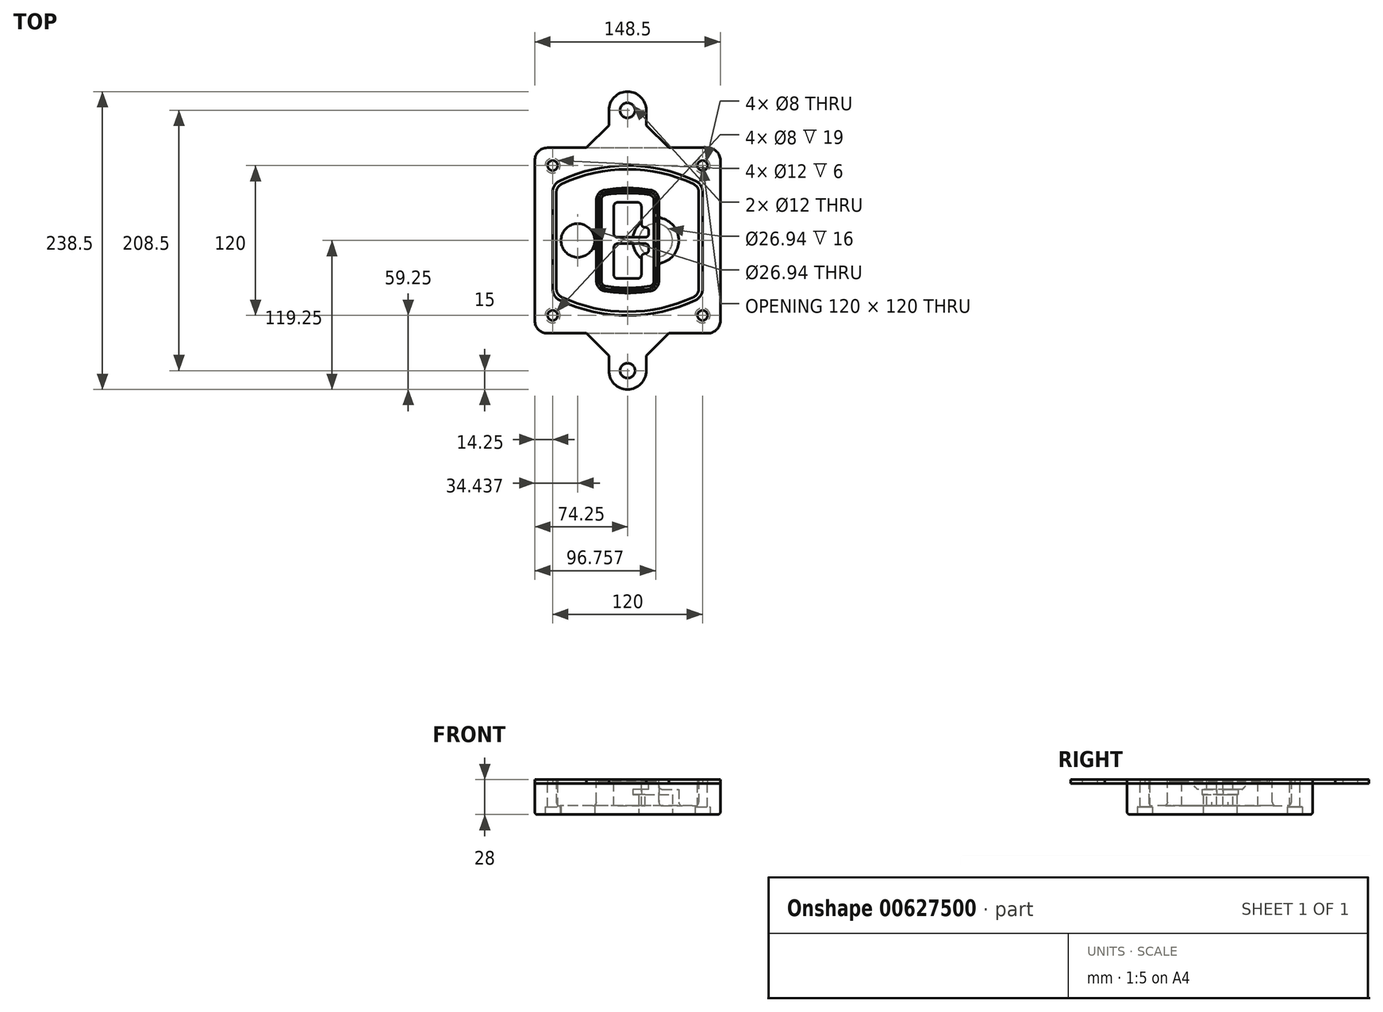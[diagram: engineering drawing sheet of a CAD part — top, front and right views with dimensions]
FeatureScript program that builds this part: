
annotation { "Feature Type Name" : "Feature", "Feature Type Description" : "" }
export const myFeature = defineFeature(function(context is Context, id is Id, definition is map)
    precondition{}
    {
        {
            var Q0;
            Q0=qCreatedBy(makeId("Top.planeOp"),FACE);
            var sketch = newSketch(context, id + "F0", { "sketchPlane" : qUnion([Q0])});
            skPoint(sketch, "E0.rect.middle", {"position": v(0, 0) * mm});
            skLineSegment(sketch, "E1.bottom", {"start": v(-64.25, -74.25) * mm, "end": v(64.25, -74.25) * mm});
            skLineSegment(sketch, "E1.top", {"start": v(-64.25, 74.25) * mm, "end": v(64.25, 74.25) * mm});
            skLineSegment(sketch, "E1.left", {"start": v(-74.25, -64.25) * mm, "end": v(-74.25, 64.25) * mm});
            skLineSegment(sketch, "E1.right", {"start": v(74.25, -64.25) * mm, "end": v(74.25, 64.25) * mm});
            skLineSegment(sketch, "E2", {"start": v(-74.25, 74.25) * mm, "end": v(74.25, -74.25) * mm, "construction": true});
            skLineSegment(sketch, "E3", {"start": v(74.25, 74.25) * mm, "end": v(-74.25, -74.25) * mm, "construction": true});
            skCircle(sketch, "E4", {"center": v(-60, 60) * mm, "radius": 4 * mm});
            skCircle(sketch, "E5", {"center": v(60, 60) * mm, "radius": 4 * mm});
            skCircle(sketch, "E6", {"center": v(60, -60) * mm, "radius": 4 * mm});
            skCircle(sketch, "E7", {"center": v(-60, -60) * mm, "radius": 4 * mm});
            skLineSegment(sketch, "E8", {"start": v(-60, 60) * mm, "end": v(60, 60) * mm, "construction": true});
            skLineSegment(sketch, "E9", {"start": v(60, 60) * mm, "end": v(60, -60) * mm, "construction": true});
            skLineSegment(sketch, "E10", {"start": v(60, -60) * mm, "end": v(-60, -60) * mm, "construction": true});
            skLineSegment(sketch, "E11", {"start": v(-60, -60) * mm, "end": v(-60, 60) * mm, "construction": true});
            skLineSegment(sketch, "E12", {"start": v(-60, 38.83) * mm, "end": v(-60, -38.83) * mm});
            skLineSegment(sketch, "E13", {"start": v(60, 38.83) * mm, "end": v(60, -38.83) * mm});
            skArc(sketch, "E14", {"start": v(54.26, 47.88) * mm, "mid": v(0, 60) * mm, "end": v(-54.26, 47.88) * mm});
            skArc(sketch, "E15", {"start": v(-54.26, -47.88) * mm, "mid": v(0, -60) * mm, "end": v(54.26, -47.88) * mm});
            skLineSegment(sketch, "E16", {"start": v(-60, 0) * mm, "end": v(60, 0) * mm, "construction": true});
            skPoint(sketch, "E17.visualSharp", {"position": v(-60, -45) * mm});
            skArc(sketch, "E17.filletArc", {"start": v(-60, -38.83) * mm, "mid": v(-58.44, -44.2) * mm, "end": v(-54.26, -47.88) * mm});
            skPoint(sketch, "E18.visualSharp", {"position": v(-60, 45) * mm});
            skArc(sketch, "E18.filletArc", {"start": v(-54.26, 47.88) * mm, "mid": v(-58.44, 44.2) * mm, "end": v(-60, 38.83) * mm});
            skPoint(sketch, "E19.visualSharp", {"position": v(60, 45) * mm});
            skArc(sketch, "E19.filletArc", {"start": v(60, 38.83) * mm, "mid": v(58.44, 44.2) * mm, "end": v(54.26, 47.88) * mm});
            skPoint(sketch, "E20.visualSharp", {"position": v(60, -45) * mm});
            skArc(sketch, "E20.filletArc", {"start": v(54.26, -47.88) * mm, "mid": v(58.44, -44.2) * mm, "end": v(60, -38.83) * mm});
            skPoint(sketch, "E21.visualSharp", {"position": v(-74.25, 74.25) * mm});
            skArc(sketch, "E21.filletArc", {"start": v(-64.25, 74.25) * mm, "mid": v(-71.32, 71.32) * mm, "end": v(-74.25, 64.25) * mm});
            skPoint(sketch, "E22.visualSharp", {"position": v(74.25, 74.25) * mm});
            skArc(sketch, "E22.filletArc", {"start": v(74.25, 64.25) * mm, "mid": v(71.32, 71.32) * mm, "end": v(64.25, 74.25) * mm});
            skPoint(sketch, "E23.visualSharp", {"position": v(74.25, -74.25) * mm});
            skArc(sketch, "E23.filletArc", {"start": v(64.25, -74.25) * mm, "mid": v(71.32, -71.32) * mm, "end": v(74.25, -64.25) * mm});
            skPoint(sketch, "E24.visualSharp", {"position": v(-74.25, -74.25) * mm});
            skArc(sketch, "E24.filletArc", {"start": v(-74.25, -64.25) * mm, "mid": v(-71.32, -71.32) * mm, "end": v(-64.25, -74.25) * mm});
            skArc(sketch, "E25.0", {"start": v(57, 38.83) * mm, "mid": v(55.9, 42.58) * mm, "end": v(52.98, 45.17) * mm});
            skLineSegment(sketch, "E25.1", {"start": v(57, 38.83) * mm, "end": v(57, -38.83) * mm});
            skArc(sketch, "E25.2", {"start": v(52.98, -45.17) * mm, "mid": v(55.9, -42.58) * mm, "end": v(57, -38.83) * mm});
            skArc(sketch, "E25.3", {"start": v(-52.98, -45.17) * mm, "mid": v(0, -57) * mm, "end": v(52.98, -45.17) * mm});
            skArc(sketch, "E25.4", {"start": v(-57, -38.83) * mm, "mid": v(-55.9, -42.58) * mm, "end": v(-52.98, -45.17) * mm});
            skArc(sketch, "E25.5", {"start": v(52.98, 45.17) * mm, "mid": v(0, 57) * mm, "end": v(-52.98, 45.17) * mm});
            skLineSegment(sketch, "E25.6", {"start": v(-57, 38.83) * mm, "end": v(-57, -38.83) * mm});
            skArc(sketch, "E25.7", {"start": v(-52.98, 45.17) * mm, "mid": v(-55.9, 42.58) * mm, "end": v(-57, 38.83) * mm});
            skArc(sketch, "E26.0", {"start": v(-55.96, 51.5) * mm, "mid": v(-61.82, 46.33) * mm, "end": v(-64, 38.83) * mm});
            skArc(sketch, "E26.1", {"start": v(55.96, 51.5) * mm, "mid": v(0, 64) * mm, "end": v(-55.96, 51.5) * mm});
            skArc(sketch, "E26.2", {"start": v(64, 38.83) * mm, "mid": v(61.82, 46.33) * mm, "end": v(55.96, 51.5) * mm});
            skLineSegment(sketch, "E26.3", {"start": v(64, 38.83) * mm, "end": v(64, -38.83) * mm});
            skArc(sketch, "E26.4", {"start": v(55.96, -51.5) * mm, "mid": v(61.82, -46.33) * mm, "end": v(64, -38.83) * mm});
            skLineSegment(sketch, "E26.5", {"start": v(-64, 38.83) * mm, "end": v(-64, -38.83) * mm});
            skArc(sketch, "E26.6", {"start": v(-55.96, -51.5) * mm, "mid": v(0, -64) * mm, "end": v(55.96, -51.5) * mm});
            skArc(sketch, "E26.7", {"start": v(-64, -38.83) * mm, "mid": v(-61.82, -46.33) * mm, "end": v(-55.96, -51.5) * mm});
            skSolve(sketch);
        }
        {
            var Q0;
            Q0=makeQuery(id+"F0.imprint","IMPRINT",FACE,{"disambiguationData":[TD([[makeQuery(id+"F0.imprint","IMPRINT",EDGE,{"derivedFrom":sQuery(id+"F0.wireOp",EDGE,"E1.bottom")}),1.0]])]});
            var Q1;
            Q1=makeQuery(id+"F0.imprint","IMPRINT",FACE,{"disambiguationData":[TD([[makeQuery(id+"F0.imprint","IMPRINT",EDGE,{"derivedFrom":sQuery(id+"F0.wireOp",EDGE,"E12")}),1.0]])]});
            var Q2;
            Q2=makeQuery(id+"F0.imprint","IMPRINT",FACE,{"disambiguationData":[TD([[makeQuery(id+"F0.imprint","IMPRINT",EDGE,{"derivedFrom":sQuery(id+"F0.wireOp",EDGE,"E25.0")}),1.0]])]});
            var Q3;
            Q3=makeQuery(id+"F0.imprint","IMPRINT",FACE,{"disambiguationData":[TD([[makeQuery(id+"F0.imprint","IMPRINT",EDGE,{"derivedFrom":sQuery(id+"F0.wireOp",EDGE,"E12")}),-1.0]])]});
            extrude(context, id + "F1", {"entities" : qUnion([Q0, Q1, Q2, Q3]), "oppositeDirection" : true, "depth" : 25 * mm});
        }
        {
            var Q0;
            Q0=makeQuery(id+"F0.imprint","IMPRINT",FACE,{"disambiguationData":[TD([[makeQuery(id+"F0.imprint","IMPRINT",EDGE,{"derivedFrom":sQuery(id+"F0.wireOp",EDGE,"E12")}),1.0]])]});
            extrude(context, id + "F2", {"entities" : qUnion([Q0]), "operationType" : NewBodyOperationType.ADD, "depth" : 3 * mm});
        }
        {
            var Q0;
            Q0=makeQuery(id+"F0.imprint","IMPRINT",FACE,{"disambiguationData":[TD([[makeQuery(id+"F0.imprint","IMPRINT",EDGE,{"derivedFrom":sQuery(id+"F0.wireOp",EDGE,"E25.0")}),1.0]])]});
            extrude(context, id + "F3", {"entities" : qUnion([Q0]), "operationType" : NewBodyOperationType.REMOVE, "oppositeDirection" : true, "depth" : 18 * mm});
        }
        {
            var Q0;
            Q0=makeQuery(id+"F2.opExtrude","CAP_FACE",FACE,{"disambiguationData":[OSD([sQuery(id+"F0.wireOp",EDGE,"E12"),sQuery(id+"F0.wireOp",EDGE,"E13"),sQuery(id+"F0.wireOp",EDGE,"E14"),sQuery(id+"F0.wireOp",EDGE,"E15"),sQuery(id+"F0.wireOp",EDGE,"E17.filletArc"),sQuery(id+"F0.wireOp",EDGE,"E18.filletArc"),sQuery(id+"F0.wireOp",EDGE,"E19.filletArc"),sQuery(id+"F0.wireOp",EDGE,"E20.filletArc"),sQuery(id+"F0.wireOp",EDGE,"E25.0"),sQuery(id+"F0.wireOp",EDGE,"E25.1"),sQuery(id+"F0.wireOp",EDGE,"E25.2"),sQuery(id+"F0.wireOp",EDGE,"E25.3"),sQuery(id+"F0.wireOp",EDGE,"E25.4"),sQuery(id+"F0.wireOp",EDGE,"E25.5"),sQuery(id+"F0.wireOp",EDGE,"E25.6"),sQuery(id+"F0.wireOp",EDGE,"E25.7")])],"isStart":false});
            var sketch = newSketch(context, id + "F4", { "sketchPlane" : qUnion([Q0])});
            skArc(sketch, "E27.0", {"start": v(-18.34, -40.45) * mm, "mid": v(0, -42) * mm, "end": v(18.34, -40.45) * mm});
            skArc(sketch, "E28.0", {"start": v(18.34, 40.45) * mm, "mid": v(0, 42) * mm, "end": v(-18.34, 40.45) * mm});
            skLineSegment(sketch, "E29", {"start": v(-25, 32.57) * mm, "end": v(-25, -32.57) * mm});
            skLineSegment(sketch, "E30", {"start": v(25, 32.57) * mm, "end": v(25, -32.57) * mm});
            skLineSegment(sketch, "E31", {"start": v(-25, 39.1) * mm, "end": v(25, 39.1) * mm, "construction": true});
            skLineSegment(sketch, "E32", {"start": v(-25, -39.1) * mm, "end": v(25, -39.1) * mm, "construction": true});
            skPoint(sketch, "E33.visualSharp", {"position": v(-25, 39.1) * mm});
            skArc(sketch, "E33.filletArc", {"start": v(-18.34, 40.45) * mm, "mid": v(-23.11, 37.73) * mm, "end": v(-25, 32.57) * mm});
            skPoint(sketch, "E34.visualSharp", {"position": v(25, 39.1) * mm});
            skArc(sketch, "E34.filletArc", {"start": v(25, 32.57) * mm, "mid": v(23.11, 37.73) * mm, "end": v(18.34, 40.45) * mm});
            skPoint(sketch, "E35.visualSharp", {"position": v(25, -39.1) * mm});
            skArc(sketch, "E35.filletArc", {"start": v(18.34, -40.45) * mm, "mid": v(23.11, -37.73) * mm, "end": v(25, -32.57) * mm});
            skPoint(sketch, "E36.visualSharp", {"position": v(-25, -39.1) * mm});
            skArc(sketch, "E36.filletArc", {"start": v(-25, -32.57) * mm, "mid": v(-23.11, -37.73) * mm, "end": v(-18.34, -40.45) * mm});
            skArc(sketch, "E37.0", {"start": v(52.98, 45.17) * mm, "mid": v(0, 57) * mm, "end": v(-52.98, 45.17) * mm});
            skArc(sketch, "E37.1", {"start": v(-52.98, 45.17) * mm, "mid": v(-55.9, 42.58) * mm, "end": v(-57, 38.83) * mm});
            skLineSegment(sketch, "E37.2", {"start": v(-57, 38.83) * mm, "end": v(-57, -38.83) * mm});
            skArc(sketch, "E37.3", {"start": v(-57, -38.83) * mm, "mid": v(-55.9, -42.58) * mm, "end": v(-52.98, -45.17) * mm});
            skArc(sketch, "E37.4", {"start": v(-52.98, -45.17) * mm, "mid": v(0, -57) * mm, "end": v(52.98, -45.17) * mm});
            skArc(sketch, "E37.5", {"start": v(52.98, -45.17) * mm, "mid": v(55.9, -42.58) * mm, "end": v(57, -38.83) * mm});
            skLineSegment(sketch, "E37.6", {"start": v(57, 38.83) * mm, "end": v(57, -38.83) * mm});
            skArc(sketch, "E37.7", {"start": v(57, 38.83) * mm, "mid": v(55.9, 42.58) * mm, "end": v(52.98, 45.17) * mm});
            skLineSegment(sketch, "E38.0", {"start": v(23, 32.57) * mm, "end": v(23, -32.57) * mm});
            skArc(sketch, "E38.1", {"start": v(18, -38.48) * mm, "mid": v(21.58, -36.44) * mm, "end": v(23, -32.57) * mm});
            skArc(sketch, "E38.2", {"start": v(-18, -38.48) * mm, "mid": v(0, -40) * mm, "end": v(18, -38.48) * mm});
            skArc(sketch, "E38.3", {"start": v(-23, -32.57) * mm, "mid": v(-21.58, -36.44) * mm, "end": v(-18, -38.48) * mm});
            skLineSegment(sketch, "E38.4", {"start": v(-23, 32.57) * mm, "end": v(-23, -32.57) * mm});
            skArc(sketch, "E38.5", {"start": v(23, 32.57) * mm, "mid": v(21.58, 36.44) * mm, "end": v(18, 38.48) * mm});
            skArc(sketch, "E38.6", {"start": v(-18, 38.48) * mm, "mid": v(-21.58, 36.44) * mm, "end": v(-23, 32.57) * mm});
            skArc(sketch, "E38.7", {"start": v(18, 38.48) * mm, "mid": v(0, 40) * mm, "end": v(-18, 38.48) * mm});
            skArc(sketch, "E39.0", {"start": v(21, 32.57) * mm, "mid": v(20.06, 35.15) * mm, "end": v(17.67, 36.5) * mm});
            skLineSegment(sketch, "E39.1", {"start": v(21, 32.57) * mm, "end": v(21, -32.57) * mm});
            skArc(sketch, "E39.2", {"start": v(17.67, -36.5) * mm, "mid": v(20.06, -35.15) * mm, "end": v(21, -32.57) * mm});
            skArc(sketch, "E39.3", {"start": v(-17.67, -36.5) * mm, "mid": v(0, -38) * mm, "end": v(17.67, -36.5) * mm});
            skArc(sketch, "E39.4", {"start": v(-21, -32.57) * mm, "mid": v(-20.06, -35.15) * mm, "end": v(-17.67, -36.5) * mm});
            skArc(sketch, "E39.5", {"start": v(17.67, 36.5) * mm, "mid": v(0, 38) * mm, "end": v(-17.67, 36.5) * mm});
            skLineSegment(sketch, "E39.6", {"start": v(-21, 32.57) * mm, "end": v(-21, -32.57) * mm});
            skArc(sketch, "E39.7", {"start": v(-17.67, 36.5) * mm, "mid": v(-20.06, 35.15) * mm, "end": v(-21, 32.57) * mm});
            skLineSegment(sketch, "E40", {"start": v(-25, 0) * mm, "end": v(25, 0) * mm, "construction": true});
            skLineSegment(sketch, "E41", {"start": v(-11, 5.5) * mm, "end": v(-11, 27.5) * mm});
            skLineSegment(sketch, "E42", {"start": v(-8, 30.5) * mm, "end": v(8, 30.5) * mm});
            skLineSegment(sketch, "E43", {"start": v(11, 27.5) * mm, "end": v(11, 13.5) * mm});
            skLineSegment(sketch, "E44", {"start": v(14, 10.5) * mm, "end": v(14, 10.5) * mm});
            skLineSegment(sketch, "E45", {"start": v(17, 7.5) * mm, "end": v(17, 5.5) * mm});
            skLineSegment(sketch, "E46", {"start": v(14, 2.5) * mm, "end": v(-8, 2.5) * mm});
            skPoint(sketch, "E47.visualSharp", {"position": v(-11, 30.5) * mm});
            skArc(sketch, "E47.filletArc", {"start": v(-8, 30.5) * mm, "mid": v(-10.12, 29.62) * mm, "end": v(-11, 27.5) * mm});
            skPoint(sketch, "E48.visualSharp", {"position": v(11, 30.5) * mm});
            skArc(sketch, "E48.filletArc", {"start": v(11, 27.5) * mm, "mid": v(10.12, 29.62) * mm, "end": v(8, 30.5) * mm});
            skPoint(sketch, "E49.visualSharp", {"position": v(11, 10.5) * mm});
            skArc(sketch, "E49.filletArc", {"start": v(11, 13.5) * mm, "mid": v(11.88, 11.38) * mm, "end": v(14, 10.5) * mm});
            skPoint(sketch, "E50.visualSharp", {"position": v(17, 10.5) * mm});
            skArc(sketch, "E50.filletArc", {"start": v(17, 7.5) * mm, "mid": v(16.12, 9.62) * mm, "end": v(14, 10.5) * mm});
            skPoint(sketch, "E51.visualSharp", {"position": v(17, 2.5) * mm});
            skArc(sketch, "E51.filletArc", {"start": v(14, 2.5) * mm, "mid": v(16.12, 3.38) * mm, "end": v(17, 5.5) * mm});
            skPoint(sketch, "E52.visualSharp", {"position": v(-11, 2.5) * mm});
            skArc(sketch, "E52.filletArc", {"start": v(-11, 5.5) * mm, "mid": v(-10.12, 3.38) * mm, "end": v(-8, 2.5) * mm});
            skLineSegment(sketch, "E53.0.MirrorCS", {"start": v(14, -2.5) * mm, "end": v(-8, -2.5) * mm});
            skArc(sketch, "E54.0.MirrorCS", {"start": v(-11, -5.5) * mm, "mid": v(-10.12, -3.38) * mm, "end": v(-8, -2.5) * mm});
            skLineSegment(sketch, "E55.0.MirrorCS", {"start": v(-11, -5.5) * mm, "end": v(-11, -27.5) * mm});
            skArc(sketch, "E56.0.MirrorCS", {"start": v(-8, -30.5) * mm, "mid": v(-10.12, -29.62) * mm, "end": v(-11, -27.5) * mm});
            skLineSegment(sketch, "E57.0.MirrorCS", {"start": v(-8, -30.5) * mm, "end": v(8, -30.5) * mm});
            skArc(sketch, "E58.0.MirrorCS", {"start": v(11, -27.5) * mm, "mid": v(10.12, -29.62) * mm, "end": v(8, -30.5) * mm});
            skLineSegment(sketch, "E59.0.MirrorCS", {"start": v(11, -27.5) * mm, "end": v(11, -13.5) * mm});
            skArc(sketch, "E60.0.MirrorCS", {"start": v(11, -13.5) * mm, "mid": v(11.88, -11.38) * mm, "end": v(14, -10.5) * mm});
            skArc(sketch, "E61.0.MirrorCS", {"start": v(17, -7.5) * mm, "mid": v(16.12, -9.62) * mm, "end": v(14, -10.5) * mm});
            skLineSegment(sketch, "E62.0.MirrorCS", {"start": v(17, -7.5) * mm, "end": v(17, -5.5) * mm});
            skArc(sketch, "E63.0.MirrorCS", {"start": v(14, -2.5) * mm, "mid": v(16.12, -3.38) * mm, "end": v(17, -5.5) * mm});
            skSolve(sketch);
        }
        {
            var Q0;
            Q0=makeQuery(id+"F4.imprint","IMPRINT",FACE,{"disambiguationData":[TD([[makeQuery(id+"F4.imprint","IMPRINT",EDGE,{"derivedFrom":sQuery(id+"F4.wireOp",EDGE,"E27.0")}),1.0]])]});
            var Q1;
            Q1=makeQuery(id+"F4.imprint","IMPRINT",FACE,{"disambiguationData":[TD([[makeQuery(id+"F4.imprint","IMPRINT",EDGE,{"derivedFrom":sQuery(id+"F4.wireOp",EDGE,"E38.0")}),-1.0]])]});
            var Q2;
            Q2=makeQuery(id+"F4.imprint","IMPRINT",FACE,{"disambiguationData":[TD([[makeQuery(id+"F4.imprint","IMPRINT",EDGE,{"derivedFrom":sQuery(id+"F4.wireOp",EDGE,"E39.0")}),1.0]])]});
            extrude(context, id + "F5", {"entities" : qUnion([Q0, Q1, Q2]), "operationType" : NewBodyOperationType.ADD, "endBound" : BoundingType.UP_TO_NEXT, "oppositeDirection" : true, "depth" : 25 * mm});
        }
        {
            var Q0;
            Q0=makeQuery(id+"F4.imprint","IMPRINT",FACE,{"disambiguationData":[TD([[makeQuery(id+"F4.imprint","IMPRINT",EDGE,{"derivedFrom":sQuery(id+"F4.wireOp",EDGE,"E38.0")}),-1.0]])]});
            extrude(context, id + "F6", {"entities" : qUnion([Q0]), "operationType" : NewBodyOperationType.REMOVE, "oppositeDirection" : true, "depth" : 2 * mm});
        }
        {
            var Q0;
            Q0=makeQuery(id+"F1.opExtrude","CAP_FACE",FACE,{"disambiguationData":[OSD([sQuery(id+"F0.wireOp",EDGE,"E1.bottom"),sQuery(id+"F0.wireOp",EDGE,"E1.top"),sQuery(id+"F0.wireOp",EDGE,"E1.left"),sQuery(id+"F0.wireOp",EDGE,"E1.right"),sQuery(id+"F0.wireOp",EDGE,"E4"),sQuery(id+"F0.wireOp",EDGE,"E5"),sQuery(id+"F0.wireOp",EDGE,"E6"),sQuery(id+"F0.wireOp",EDGE,"E7"),sQuery(id+"F0.wireOp",EDGE,"E21.filletArc"),sQuery(id+"F0.wireOp",EDGE,"E22.filletArc"),sQuery(id+"F0.wireOp",EDGE,"E23.filletArc"),sQuery(id+"F0.wireOp",EDGE,"E24.filletArc")])],"isStart":false});
            var sketch = newSketch(context, id + "F7", { "sketchPlane" : qUnion([Q0])});
            skCircle(sketch, "E64", {"center": v(22.5, 0) * mm, "radius": 13.47 * mm});
            skCircle(sketch, "E65", {"center": v(-39.81, 0) * mm, "radius": 13.47 * mm});
            skLineSegment(sketch, "E66", {"start": v(74.25, 0) * mm, "end": v(-74.25, 0) * mm});
            skCircle(sketch, "E67", {"center": v(22.5, 0) * mm, "radius": 18.47 * mm});
            skCircle(sketch, "E68", {"center": v(60, -60) * mm, "radius": 6 * mm});
            skCircle(sketch, "E69", {"center": v(-60, -60) * mm, "radius": 6 * mm});
            skCircle(sketch, "E70", {"center": v(-60, 60) * mm, "radius": 6 * mm});
            skCircle(sketch, "E71", {"center": v(60, 60) * mm, "radius": 6 * mm});
            skSolve(sketch);
        }
        {
            var Q0;
            {var subQ1=sQuery(id+"F7.wireOp",EDGE,"E66");var subQ4=sQuery(id+"F7.wireOp",EDGE,"E64");var subQ6=makeQuery(id+"F7.imprint","INTERSECT",VERTEX,{"disambiguationData":[OD(0.0)],"derivedFrom":[subQ4,subQ1]});Q0=makeQuery(id+"F7.imprint","IMPRINT",FACE,{"disambiguationData":[TD([[makeQuery(id+"F7.imprint","IMPRINT",EDGE,{"disambiguationData":[TD([[subQ6,-1.0]])],"derivedFrom":subQ4}),-1.0]])]});}
            var Q1;
            {var subQ0=sQuery(id+"F7.wireOp",EDGE,"E66");var subQ1=sQuery(id+"F7.wireOp",EDGE,"E64");var subQ3=makeQuery(id+"F7.imprint","INTERSECT",VERTEX,{"disambiguationData":[OD(0.0)],"derivedFrom":[subQ1,subQ0]});Q1=makeQuery(id+"F7.imprint","IMPRINT",FACE,{"disambiguationData":[TD([[makeQuery(id+"F7.imprint","IMPRINT",EDGE,{"disambiguationData":[TD([[subQ3,-1.0]])],"derivedFrom":subQ1}),1.0]])]});}
            var Q2;
            {var subQ0=sQuery(id+"F7.wireOp",EDGE,"E66");var subQ1=sQuery(id+"F7.wireOp",EDGE,"E64");var subQ3=makeQuery(id+"F7.imprint","INTERSECT",VERTEX,{"disambiguationData":[OD(0.0)],"derivedFrom":[subQ1,subQ0]});Q2=makeQuery(id+"F7.imprint","IMPRINT",FACE,{"disambiguationData":[TD([[makeQuery(id+"F7.imprint","IMPRINT",EDGE,{"disambiguationData":[TD([[subQ3,1.0]])],"derivedFrom":subQ1}),1.0]])]});}
            var Q3;
            {var subQ1=sQuery(id+"F7.wireOp",EDGE,"E66");var subQ4=sQuery(id+"F7.wireOp",EDGE,"E64");var subQ6=makeQuery(id+"F7.imprint","INTERSECT",VERTEX,{"disambiguationData":[OD(0.0)],"derivedFrom":[subQ4,subQ1]});Q3=makeQuery(id+"F7.imprint","IMPRINT",FACE,{"disambiguationData":[TD([[makeQuery(id+"F7.imprint","IMPRINT",EDGE,{"disambiguationData":[TD([[subQ6,1.0]])],"derivedFrom":subQ4}),-1.0]])]});}
            extrude(context, id + "F8", {"entities" : qUnion([Q0, Q1, Q2, Q3]), "operationType" : NewBodyOperationType.ADD, "oppositeDirection" : true, "depth" : 20 * mm});
        }
        {
            var Q0;
            {var subQ0=sQuery(id+"F7.wireOp",EDGE,"E66");var subQ1=sQuery(id+"F7.wireOp",EDGE,"E64");var subQ3=makeQuery(id+"F7.imprint","INTERSECT",VERTEX,{"disambiguationData":[OD(0.0)],"derivedFrom":[subQ1,subQ0]});Q0=makeQuery(id+"F7.imprint","IMPRINT",FACE,{"disambiguationData":[TD([[makeQuery(id+"F7.imprint","IMPRINT",EDGE,{"disambiguationData":[TD([[subQ3,-1.0]])],"derivedFrom":subQ1}),1.0]])]});}
            var Q1;
            {var subQ0=sQuery(id+"F7.wireOp",EDGE,"E66");var subQ1=sQuery(id+"F7.wireOp",EDGE,"E64");var subQ3=makeQuery(id+"F7.imprint","INTERSECT",VERTEX,{"disambiguationData":[OD(0.0)],"derivedFrom":[subQ1,subQ0]});Q1=makeQuery(id+"F7.imprint","IMPRINT",FACE,{"disambiguationData":[TD([[makeQuery(id+"F7.imprint","IMPRINT",EDGE,{"disambiguationData":[TD([[subQ3,1.0]])],"derivedFrom":subQ1}),1.0]])]});}
            extrude(context, id + "F9", {"entities" : qUnion([Q0, Q1]), "operationType" : NewBodyOperationType.REMOVE, "oppositeDirection" : true, "depth" : 16 * mm});
        }
        {
            var Q0;
            {var subQ0=sQuery(id+"F7.wireOp",EDGE,"E66");var subQ1=sQuery(id+"F7.wireOp",EDGE,"E65");var subQ3=makeQuery(id+"F7.imprint","INTERSECT",VERTEX,{"disambiguationData":[OD(0.0)],"derivedFrom":[subQ1,subQ0]});Q0=makeQuery(id+"F7.imprint","IMPRINT",FACE,{"disambiguationData":[TD([[makeQuery(id+"F7.imprint","IMPRINT",EDGE,{"disambiguationData":[TD([[subQ3,-1.0]])],"derivedFrom":subQ1}),1.0]])]});}
            var Q1;
            {var subQ0=sQuery(id+"F7.wireOp",EDGE,"E66");var subQ1=sQuery(id+"F7.wireOp",EDGE,"E65");var subQ3=makeQuery(id+"F7.imprint","INTERSECT",VERTEX,{"disambiguationData":[OD(0.0)],"derivedFrom":[subQ1,subQ0]});Q1=makeQuery(id+"F7.imprint","IMPRINT",FACE,{"disambiguationData":[TD([[makeQuery(id+"F7.imprint","IMPRINT",EDGE,{"disambiguationData":[TD([[subQ3,1.0]])],"derivedFrom":subQ1}),1.0]])]});}
            extrude(context, id + "F10", {"entities" : qUnion([Q0, Q1]), "operationType" : NewBodyOperationType.REMOVE, "oppositeDirection" : true, "depth" : 25 * mm});
        }
        {
            var Q0;
            Q0=makeQuery(id+"F7.imprint","IMPRINT",FACE,{"disambiguationData":[TD([[makeQuery(id+"F7.imprint","IMPRINT",EDGE,{"derivedFrom":sQuery(id+"F7.wireOp",EDGE,"E68")}),1.0]])]});
            var Q1;
            Q1=makeQuery(id+"F7.imprint","IMPRINT",FACE,{"disambiguationData":[TD([[makeQuery(id+"F7.imprint","IMPRINT",EDGE,{"derivedFrom":makeQuery(id+"F1.opExtrude","CAP_EDGE",EDGE,{"disambiguationData":[OSD([sQuery(id+"F0.wireOp",EDGE,"E5")])],"isStart":false})}),-1.0]])]});
            var Q2;
            Q2=makeQuery(id+"F7.imprint","IMPRINT",FACE,{"disambiguationData":[TD([[makeQuery(id+"F7.imprint","IMPRINT",EDGE,{"derivedFrom":sQuery(id+"F7.wireOp",EDGE,"E69")}),1.0]])]});
            var Q3;
            Q3=makeQuery(id+"F7.imprint","IMPRINT",FACE,{"disambiguationData":[TD([[makeQuery(id+"F7.imprint","IMPRINT",EDGE,{"derivedFrom":makeQuery(id+"F1.opExtrude","CAP_EDGE",EDGE,{"disambiguationData":[OSD([sQuery(id+"F0.wireOp",EDGE,"E4")])],"isStart":false})}),-1.0]])]});
            var Q4;
            Q4=makeQuery(id+"F7.imprint","IMPRINT",FACE,{"disambiguationData":[TD([[makeQuery(id+"F7.imprint","IMPRINT",EDGE,{"derivedFrom":sQuery(id+"F7.wireOp",EDGE,"E70")}),1.0]])]});
            var Q5;
            Q5=makeQuery(id+"F7.imprint","IMPRINT",FACE,{"disambiguationData":[TD([[makeQuery(id+"F7.imprint","IMPRINT",EDGE,{"derivedFrom":makeQuery(id+"F1.opExtrude","CAP_EDGE",EDGE,{"disambiguationData":[OSD([sQuery(id+"F0.wireOp",EDGE,"E7")])],"isStart":false})}),-1.0]])]});
            var Q6;
            Q6=makeQuery(id+"F7.imprint","IMPRINT",FACE,{"disambiguationData":[TD([[makeQuery(id+"F7.imprint","IMPRINT",EDGE,{"derivedFrom":sQuery(id+"F7.wireOp",EDGE,"E71")}),1.0]])]});
            var Q7;
            Q7=makeQuery(id+"F7.imprint","IMPRINT",FACE,{"disambiguationData":[TD([[makeQuery(id+"F7.imprint","IMPRINT",EDGE,{"derivedFrom":makeQuery(id+"F1.opExtrude","CAP_EDGE",EDGE,{"disambiguationData":[OSD([sQuery(id+"F0.wireOp",EDGE,"E6")])],"isStart":false})}),-1.0]])]});
            extrude(context, id + "F11", {"entities" : qUnion([Q0, Q1, Q2, Q3, Q4, Q5, Q6, Q7]), "operationType" : NewBodyOperationType.REMOVE, "oppositeDirection" : true, "depth" : 6 * mm});
        }
        {
            var Q0;
            Q0=makeQuery(id+"F9.boolean.opBoolean","COPY",FACE,{"derivedFrom":makeQuery(id+"F9.opExtrude","CAP_FACE",FACE,{"disambiguationData":[OSD([sQuery(id+"F7.wireOp",EDGE,"E64")])],"isStart":false})});
            var sketch = newSketch(context, id + "F12", { "sketchPlane" : qUnion([Q0])});
            skArc(sketch, "E72.0", {"start": v(11, 14.45) * mm, "mid": v(6.45, 9.13) * mm, "end": v(4.2, 2.5) * mm});
            skArc(sketch, "E72.1", {"start": v(4.2, -2.5) * mm, "mid": v(6.45, -9.13) * mm, "end": v(11, -14.45) * mm});
            skLineSegment(sketch, "E73", {"start": v(4.2, -2.5) * mm, "end": v(14, -2.5) * mm});
            skLineSegment(sketch, "E74.0", {"start": v(14, 2.5) * mm, "end": v(4.2, 2.5) * mm});
            skArc(sketch, "E74.1", {"start": v(14, 2.5) * mm, "mid": v(16.12, 3.38) * mm, "end": v(17, 5.5) * mm});
            skLineSegment(sketch, "E74.2", {"start": v(17, 7.5) * mm, "end": v(17, 5.5) * mm});
            skArc(sketch, "E74.3", {"start": v(17, 7.5) * mm, "mid": v(16.12, 9.62) * mm, "end": v(14, 10.5) * mm});
            skArc(sketch, "E74.4", {"start": v(11, 13.5) * mm, "mid": v(11.88, 11.38) * mm, "end": v(14, 10.5) * mm});
            skLineSegment(sketch, "E74.5", {"start": v(11, 14.45) * mm, "end": v(11, 13.5) * mm});
            skLineSegment(sketch, "E74.7", {"start": v(14, -2.5) * mm, "end": v(4.2, -2.5) * mm});
            skArc(sketch, "E74.8", {"start": v(14, -2.5) * mm, "mid": v(16.12, -3.38) * mm, "end": v(17, -5.5) * mm});
            skLineSegment(sketch, "E74.9", {"start": v(17, -7.5) * mm, "end": v(17, -5.5) * mm});
            skArc(sketch, "E74.10", {"start": v(17, -7.5) * mm, "mid": v(16.12, -9.62) * mm, "end": v(14, -10.5) * mm});
            skArc(sketch, "E74.11", {"start": v(11, -13.5) * mm, "mid": v(11.88, -11.38) * mm, "end": v(14, -10.5) * mm});
            skLineSegment(sketch, "E74.12", {"start": v(11, -14.45) * mm, "end": v(11, -13.5) * mm});
            skPoint(sketch, "E75.orphan", {"position": v(11, -27.5) * mm});
            skPoint(sketch, "E76.orphan", {"position": v(-8, -2.5) * mm});
            skPoint(sketch, "E77.orphan", {"position": v(-8, 2.5) * mm});
            skPoint(sketch, "E78.orphan", {"position": v(11, 27.5) * mm});
            skSolve(sketch);
        }
        {
            var Q0;
            {var subQ7=sQuery(id+"F12.wireOp",EDGE,"E72.0");var subQ14=sQuery(id+"F12.wireOp",EDGE,"E72.1");var subQ16=sQuery(id+"F12.wireOp",EDGE,"E74.1");var subQ18=sQuery(id+"F12.wireOp",EDGE,"E74.8");Q0=qUnion([makeQuery(id+"F12.imprint","IMPRINT",FACE,{"disambiguationData":[TD([[makeQuery(id+"F12.imprint","IMPRINT",EDGE,{"derivedFrom":subQ7}),1.0]])]}),makeQuery(id+"F12.imprint","IMPRINT",FACE,{"disambiguationData":[TD([[makeQuery(id+"F12.imprint","IMPRINT",EDGE,{"derivedFrom":subQ14}),1.0]])]}),makeQuery(id+"F12.imprint","IMPRINT",FACE,{"disambiguationData":[TD([[makeQuery(id+"F12.imprint","IMPRINT",EDGE,{"derivedFrom":subQ16}),1.0]])]}),makeQuery(id+"F12.imprint","IMPRINT",FACE,{"disambiguationData":[TD([[makeQuery(id+"F12.imprint","IMPRINT",EDGE,{"derivedFrom":subQ18}),-1.0]])]})]);}
            var Q1;
            Q1=makeQuery(id+"F5.boolean.opBoolean","SPLIT",FACE,{"disambiguationData":[TD([makeQuery(id+"F5.opExtrude","SWEPT_FACE",FACE,{"disambiguationData":[OSD([sQuery(id+"F4.wireOp",EDGE,"E41")])]})])],"derivedFrom":makeQuery(id+"F3.boolean.opBoolean","COPY",FACE,{"derivedFrom":makeQuery(id+"F3.opExtrude","CAP_FACE",FACE,{"disambiguationData":[OSD([sQuery(id+"F0.wireOp",EDGE,"E25.0"),sQuery(id+"F0.wireOp",EDGE,"E25.1"),sQuery(id+"F0.wireOp",EDGE,"E25.2"),sQuery(id+"F0.wireOp",EDGE,"E25.3"),sQuery(id+"F0.wireOp",EDGE,"E25.4"),sQuery(id+"F0.wireOp",EDGE,"E25.5"),sQuery(id+"F0.wireOp",EDGE,"E25.6"),sQuery(id+"F0.wireOp",EDGE,"E25.7")])],"isStart":false})})});
            extrude(context, id + "F13", {"entities" : qUnion([Q0]), "operationType" : NewBodyOperationType.REMOVE, "endBound" : BoundingType.UP_TO_SURFACE, "endBoundEntityFace" : qUnion([Q1]), "depth" : 25 * mm});
        }
        {
            var Q0;
            Q0=makeQuery(id+"F3.boolean.opBoolean","COPY",EDGE,{"derivedFrom":makeQuery(id+"F3.opExtrude","CAP_EDGE",EDGE,{"disambiguationData":[OSD([sQuery(id+"F0.wireOp",EDGE,"E25.6")])],"isStart":false})});
            var Q1;
            Q1=makeQuery(id+"F8.boolean.opBoolean","INTERSECT",EDGE,{"derivedFrom":[makeQuery(id+"F5.opExtrude","SWEPT_FACE",FACE,{"disambiguationData":[OSD([sQuery(id+"F4.wireOp",EDGE,"E30")])]}),makeQuery(id+"F8.opExtrude","CAP_FACE",FACE,{"disambiguationData":[OSD([sQuery(id+"F7.wireOp",EDGE,"E67")])],"isStart":false})]});
            var Q2;
            Q2=makeQuery(id+"F8.boolean.opBoolean","INTERSECT",EDGE,{"disambiguationData":[OD(1.0)],"derivedFrom":[makeQuery(id+"F5.opExtrude","SWEPT_FACE",FACE,{"disambiguationData":[OSD([sQuery(id+"F4.wireOp",EDGE,"E30")])]}),makeQuery(id+"F8.opExtrude","SWEPT_FACE",FACE,{"disambiguationData":[OSD([sQuery(id+"F7.wireOp",EDGE,"E67")])]})]});
            var Q3;
            {var subQ0=sQuery(id+"F4.wireOp",EDGE,"E30");Q3=makeQuery(id+"F8.boolean.opBoolean","SPLIT",EDGE,{"disambiguationData":[TD([makeQuery(id+"F5.opExtrude","SWEPT_FACE",FACE,{"disambiguationData":[OSD([sQuery(id+"F4.wireOp",EDGE,"E35.filletArc")])]})])],"derivedFrom":makeQuery(id+"F5.opExtrude","CAP_EDGE",EDGE,{"disambiguationData":[OSD([subQ0])],"isStart":false})});}
            var Q4;
            {var subQ0=sQuery(id+"F0.wireOp",EDGE,"E25.7");var subQ1=sQuery(id+"F0.wireOp",EDGE,"E25.1");var subQ2=sQuery(id+"F0.wireOp",EDGE,"E25.6");var subQ3=sQuery(id+"F0.wireOp",EDGE,"E25.5");var subQ4=sQuery(id+"F0.wireOp",EDGE,"E25.4");var subQ5=sQuery(id+"F0.wireOp",EDGE,"E25.0");var subQ6=sQuery(id+"F0.wireOp",EDGE,"E25.2");var subQ7=sQuery(id+"F0.wireOp",EDGE,"E25.3");Q4=makeQuery(id+"F8.boolean.opBoolean","INTERSECT",EDGE,{"derivedFrom":[makeQuery(id+"F5.boolean.opBoolean","SPLIT",FACE,{"disambiguationData":[TD([makeQuery(id+"F2.opExtrude","SWEPT_FACE",FACE,{"disambiguationData":[OSD([subQ5])]})])],"derivedFrom":makeQuery(id+"F3.boolean.opBoolean","COPY",FACE,{"derivedFrom":makeQuery(id+"F3.opExtrude","CAP_FACE",FACE,{"disambiguationData":[OSD([subQ5,subQ1,subQ6,subQ7,subQ4,subQ3,subQ2,subQ0])],"isStart":false})})}),makeQuery(id+"F8.opExtrude","SWEPT_FACE",FACE,{"disambiguationData":[OSD([sQuery(id+"F7.wireOp",EDGE,"E67")])]})]});}
            var Q5;
            Q5=makeQuery(id+"F8.boolean.opBoolean","INTERSECT",EDGE,{"disambiguationData":[OD(0.0)],"derivedFrom":[makeQuery(id+"F5.opExtrude","SWEPT_FACE",FACE,{"disambiguationData":[OSD([sQuery(id+"F4.wireOp",EDGE,"E30")])]}),makeQuery(id+"F8.opExtrude","SWEPT_FACE",FACE,{"disambiguationData":[OSD([sQuery(id+"F7.wireOp",EDGE,"E67")])]})]});
            fillet(context, id + "F14", {"entities" : qUnion([Q0, Q1, Q2, Q3, Q4, Q5]), "radius" : 3 * mm, "tangentPropagation" : true, "allowEdgeOverflow" : false});
        }
        {
            var Q0;
            Q0=makeQuery(id+"F1.opExtrude","CAP_EDGE",EDGE,{"disambiguationData":[OSD([sQuery(id+"F0.wireOp",EDGE,"E1.bottom")])],"isStart":false});
            fillet(context, id + "F15", {"entities" : qUnion([Q0]), "radius" : 2 * mm, "tangentPropagation" : true, "allowEdgeOverflow" : false});
        }
        {
            var Q0;
            {var subQ0=sQuery(id+"F0.wireOp",EDGE,"E21.filletArc");var subQ1=sQuery(id+"F0.wireOp",EDGE,"E7");var subQ2=sQuery(id+"F0.wireOp",EDGE,"E6");var subQ3=sQuery(id+"F0.wireOp",EDGE,"E5");var subQ4=sQuery(id+"F0.wireOp",EDGE,"E4");var subQ5=sQuery(id+"F0.wireOp",EDGE,"E22.filletArc");var subQ6=sQuery(id+"F0.wireOp",EDGE,"E1.bottom");var subQ7=sQuery(id+"F0.wireOp",EDGE,"E1.right");var subQ8=sQuery(id+"F0.wireOp",EDGE,"E1.top");var subQ9=sQuery(id+"F0.wireOp",EDGE,"E1.left");var subQ10=sQuery(id+"F0.wireOp",EDGE,"E23.filletArc");var subQ11=sQuery(id+"F0.wireOp",EDGE,"E24.filletArc");Q0=makeQuery(id+"F2.boolean.opBoolean","SPLIT",FACE,{"disambiguationData":[TD([makeQuery(id+"F1.opExtrude","SWEPT_FACE",FACE,{"disambiguationData":[OSD([subQ6])]})])],"derivedFrom":makeQuery(id+"F1.opExtrude","CAP_FACE",FACE,{"disambiguationData":[OSD([subQ6,subQ8,subQ9,subQ7,subQ4,subQ3,subQ2,subQ1,subQ0,subQ5,subQ10,subQ11])],"isStart":true})});}
            var sketch = newSketch(context, id + "F16", { "sketchPlane" : qUnion([Q0])});
            skLineSegment(sketch, "E79", {"start": v(-33, 74.25) * mm, "end": v(-15, 92.25) * mm});
            skLineSegment(sketch, "E80", {"start": v(33, 74.25) * mm, "end": v(15, 92.25) * mm});
            skLineSegment(sketch, "E81", {"start": v(-15, 92.25) * mm, "end": v(-15, 104.25) * mm});
            skLineSegment(sketch, "E82", {"start": v(15, 92.25) * mm, "end": v(15, 104.25) * mm});
            skArc(sketch, "E83", {"start": v(15, 104.25) * mm, "mid": v(0, 119.25) * mm, "end": v(-15, 104.25) * mm});
            skCircle(sketch, "E84", {"center": v(0, 104.25) * mm, "radius": 6 * mm});
            skLineSegment(sketch, "E85", {"start": v(0, 104.25) * mm, "end": v(0, 74.25) * mm});
            skLineSegment(sketch, "E86", {"start": v(-74.25, 0) * mm, "end": v(74.25, 0) * mm, "construction": true});
            skLineSegment(sketch, "E87.MirrorCS", {"start": v(-15, -92.25) * mm, "end": v(-15, -104.25) * mm});
            skLineSegment(sketch, "E88.MirrorCS", {"start": v(15, -92.25) * mm, "end": v(15, -104.25) * mm});
            skArc(sketch, "E89.MirrorCS", {"start": v(15, -104.25) * mm, "mid": v(0, -119.25) * mm, "end": v(-15, -104.25) * mm});
            skCircle(sketch, "E90.MirrorC", {"center": v(0, -104.25) * mm, "radius": 6 * mm});
            skLineSegment(sketch, "E91.MirrorCS", {"start": v(0, -104.25) * mm, "end": v(0, -74.25) * mm});
            skLineSegment(sketch, "E92.MirrorCS", {"start": v(-33, -74.25) * mm, "end": v(-15, -92.25) * mm});
            skLineSegment(sketch, "E93.MirrorCS", {"start": v(33, -74.25) * mm, "end": v(15, -92.25) * mm});
            skSolve(sketch);
        }
        {
            var Q0;
            Q0=makeQuery(id+"F16.imprint","IMPRINT",FACE,{"disambiguationData":[TD([[makeQuery(id+"F16.imprint","IMPRINT",EDGE,{"derivedFrom":sQuery(id+"F16.wireOp",EDGE,"E87.MirrorCS")}),1.0]])]});
            var Q1;
            Q1=makeQuery(id+"F16.imprint","IMPRINT",FACE,{"disambiguationData":[TD([[makeQuery(id+"F16.imprint","IMPRINT",EDGE,{"derivedFrom":makeQuery(id+"F1.opExtrude","CAP_EDGE",EDGE,{"disambiguationData":[OSD([sQuery(id+"F0.wireOp",EDGE,"E1.left")])],"isStart":true})}),-1.0]])]});
            var Q2;
            {var subQ0=sQuery(id+"F16.wireOp",EDGE,"E79");Q2=makeQuery(id+"F16.imprint","IMPRINT",FACE,{"disambiguationData":[TD([[makeQuery(id+"F16.imprint","IMPRINT",EDGE,{"derivedFrom":subQ0}),-1.0]])]});}
            var Q3;
            Q3=makeQuery(id+"F2.opExtrude","CAP_FACE",FACE,{"disambiguationData":[OSD([sQuery(id+"F0.wireOp",EDGE,"E12"),sQuery(id+"F0.wireOp",EDGE,"E13"),sQuery(id+"F0.wireOp",EDGE,"E14"),sQuery(id+"F0.wireOp",EDGE,"E15"),sQuery(id+"F0.wireOp",EDGE,"E17.filletArc"),sQuery(id+"F0.wireOp",EDGE,"E18.filletArc"),sQuery(id+"F0.wireOp",EDGE,"E19.filletArc"),sQuery(id+"F0.wireOp",EDGE,"E20.filletArc"),sQuery(id+"F0.wireOp",EDGE,"E25.0"),sQuery(id+"F0.wireOp",EDGE,"E25.1"),sQuery(id+"F0.wireOp",EDGE,"E25.2"),sQuery(id+"F0.wireOp",EDGE,"E25.3"),sQuery(id+"F0.wireOp",EDGE,"E25.4"),sQuery(id+"F0.wireOp",EDGE,"E25.5"),sQuery(id+"F0.wireOp",EDGE,"E25.6"),sQuery(id+"F0.wireOp",EDGE,"E25.7")])],"isStart":false});
            extrude(context, id + "F17", {"entities" : qUnion([Q0, Q1, Q2]), "endBound" : BoundingType.UP_TO_SURFACE, "depth" : 6 * mm, "endBoundEntityFace" : qUnion([Q3]), "offsetDistance" : 25 * mm});
        }
    });
